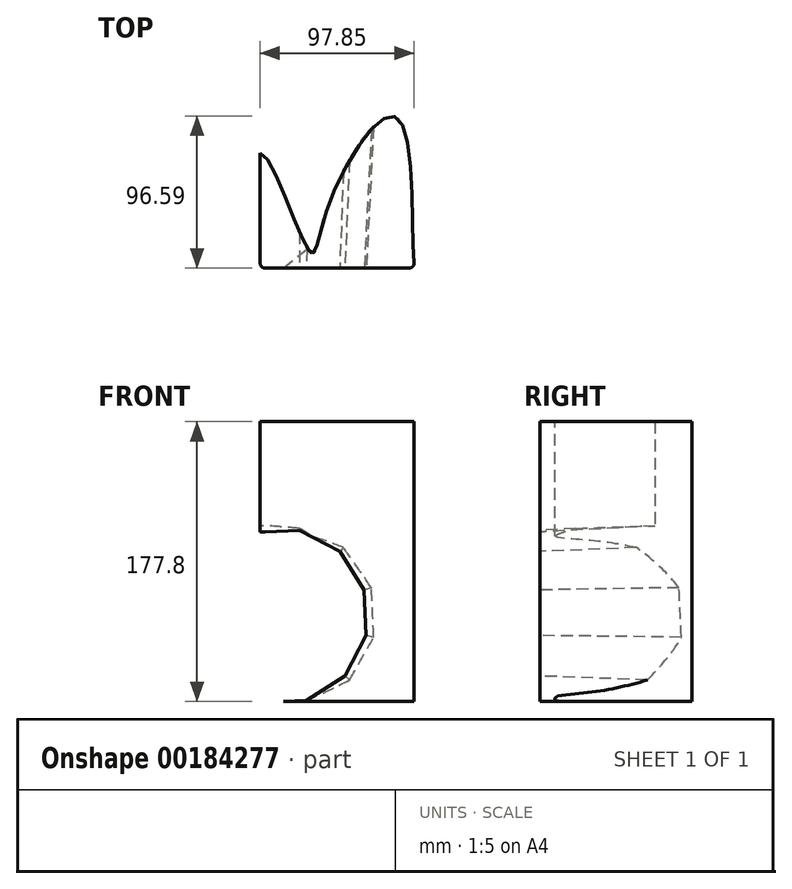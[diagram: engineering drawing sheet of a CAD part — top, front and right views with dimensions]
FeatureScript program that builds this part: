
annotation { "Feature Type Name" : "Feature", "Feature Type Description" : "" }
export const myFeature = defineFeature(function(context is Context, id is Id, definition is map)
    precondition{}
    {
        {
            var Q0;
            Q0=qCreatedBy(makeId("Top.planeOp"),FACE);
            var sketch = newSketch(context, id + "F0", { "sketchPlane" : qUnion([Q0])});
            skLineSegment(sketch, "E0", {"start": v(-67.39, 12.94) * mm, "end": v(-67.39, -56.91) * mm});
            skLineSegment(sketch, "E1", {"start": v(-64.21, -60.09) * mm, "end": v(27.28, -60.09) * mm});
            skPoint(sketch, "E2.end.orphan", {"position": v(31.04, 16.11) * mm});
            skFitSpline(sketch, "E3", {"points": [v(-67.39, 12.94) * mm, v(-35.93, -49.58) * mm, v(-24.56, -22.09) * mm, v(19.98, 35.1) * mm, v(31.04, -60.09) * mm], "startDerivative": vector(96.1, -9.02) * mm, "endDerivative": vector(32.22, -117.42) * mm});
            skPoint(sketch, "E4.visualSharp", {"position": v(-67.39, -60.09) * mm});
            skArc(sketch, "E4.filletArc", {"start": v(-67.39, -56.91) * mm, "mid": v(-66.46, -59.16) * mm, "end": v(-64.21, -60.09) * mm});
            skArc(sketch, "E5.filletArc", {"start": v(27.28, -60.09) * mm, "mid": v(29.65, -59.03) * mm, "end": v(30.44, -56.56) * mm});
            skSolve(sketch);
        }
        {
            var Q0;
            Q0=makeQuery(id+"F0.imprint","IMPRINT",FACE,{"disambiguationData":[TD([[makeQuery(id+"F0.imprint","IMPRINT",EDGE,{"derivedFrom":sQuery(id+"F0.wireOp",EDGE,"E0")}),1.0]])]});
            extrude(context, id + "F1", {"entities" : qUnion([Q0]), "depth" : 177.8 * mm});
        }
        {
            var Q0;
            Q0=makeQuery(id+"F1.opExtrude","SWEPT_FACE",FACE,{"disambiguationData":[OSD([sQuery(id+"F0.wireOp",EDGE,"E1")])]});
            var sketch = newSketch(context, id + "F2", { "sketchPlane" : qUnion([Q0])});
            skCircle(sketch, "E6.cCircle", {"center": v(-54.67, 54.07) * mm, "radius": 54.11 * mm, "construction": true});
            skLineSegment(sketch, "E6.0", {"start": v(-42.47, 108.75) * mm, "end": v(-16.76, 95.32) * mm});
            skLineSegment(sketch, "E6.1", {"start": v(-16.76, 95.32) * mm, "end": v(-1.22, 70.85) * mm});
            skLineSegment(sketch, "E6.2", {"start": v(-1.22, 70.85) * mm, "end": v(0, 41.87) * mm});
            skLineSegment(sketch, "E6.3", {"start": v(0, 41.87) * mm, "end": v(-13.42, 16.17) * mm});
            skLineSegment(sketch, "E6.4", {"start": v(-13.42, 16.17) * mm, "end": v(-37.9, 0.62) * mm});
            skLineSegment(sketch, "E6.5", {"start": v(-37.9, 0.62) * mm, "end": v(-66.87, -0.6) * mm});
            skLineSegment(sketch, "E6.6", {"start": v(-66.87, -0.6) * mm, "end": v(-92.57, 12.82) * mm});
            skLineSegment(sketch, "E6.7", {"start": v(-92.57, 12.82) * mm, "end": v(-108.12, 37.3) * mm});
            skLineSegment(sketch, "E6.8", {"start": v(-108.12, 37.3) * mm, "end": v(-109.34, 66.27) * mm});
            skLineSegment(sketch, "E6.9", {"start": v(-109.34, 66.27) * mm, "end": v(-95.92, 91.98) * mm});
            skLineSegment(sketch, "E6.10", {"start": v(-95.92, 91.98) * mm, "end": v(-71.44, 107.52) * mm});
            skLineSegment(sketch, "E6.11", {"start": v(-71.44, 107.52) * mm, "end": v(-42.47, 108.75) * mm});
            skPoint(sketch, "E6.0.midPoint", {"position": v(-29.62, 102.04) * mm});
            skSolve(sketch);
        }
        {
            var Q0;
            {var subQ0=sQuery(id+"F2.wireOp",EDGE,"E6.6");Q0=makeQuery(id+"F2.imprint","IMPRINT",FACE,{"disambiguationData":[TD([[makeQuery(id+"F2.imprint","IMPRINT",EDGE,{"derivedFrom":subQ0}),-1.0]])]});}
            var Q1;
            {var subQ6=sQuery(id+"F2.wireOp",EDGE,"E6.0");Q1=makeQuery(id+"F2.imprint","IMPRINT",FACE,{"disambiguationData":[TD([[makeQuery(id+"F2.imprint","IMPRINT",EDGE,{"derivedFrom":subQ6}),-1.0]])]});}
            extrude(context, id + "F3", {"entities" : qUnion([Q0, Q1]), "operationType" : NewBodyOperationType.REMOVE, "oppositeDirection" : true, "depth" : 254 * mm, "hasDraft" : true, "draftAngle" : 3 * degree});
        }
    });
